AUTODESK INVENTOR PART (.ipt)
format: ipt  version: 2025 (Build 290162000, 162)  size: 84,480 bytes
history: native  units: mm
features: other x2, revolve x1, sketch x1, reference x1
ambient origin geometry x8: Origin, YZ Plane, XZ Plane, XY Plane, X Axis, Y Axis, Z Axis, Center Point
bodies: Body1 (feature_tree)
feature tree (5):
  revolve  "旋转2"  Angle=90.0deg
  sketch  "草图2"  dims[d3=12.5mm d4=90.0deg]
  reference  "参考2"
  other  "齿轮箱.iam"
  other  "高速轴承透盖"
